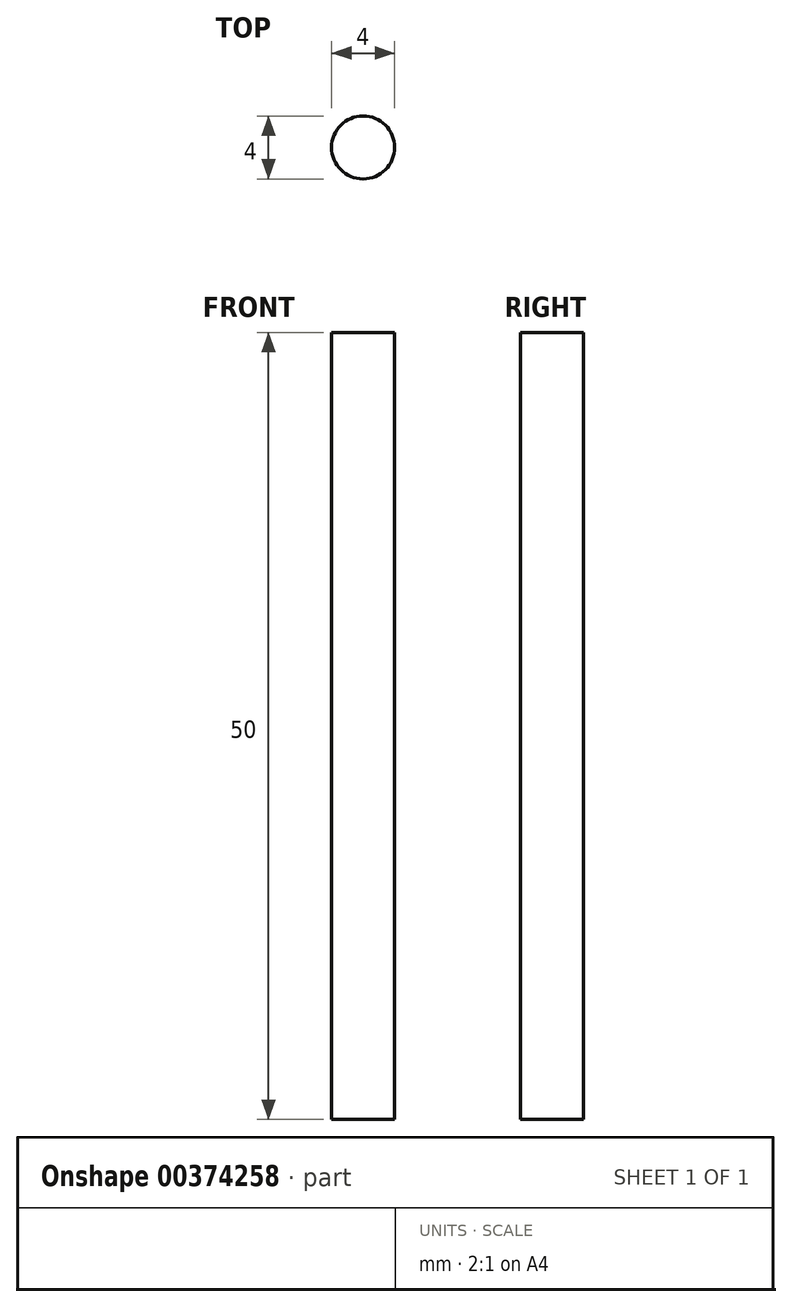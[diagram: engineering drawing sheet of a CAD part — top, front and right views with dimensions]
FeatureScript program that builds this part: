
annotation { "Feature Type Name" : "Feature", "Feature Type Description" : "" }
export const myFeature = defineFeature(function(context is Context, id is Id, definition is map)
    precondition{}
    {
        {
            var Q0;
            Q0=qCreatedBy(makeId("Top.planeOp"),FACE);
            var sketch = newSketch(context, id + "F0", { "sketchPlane" : qUnion([Q0])});
            skCircle(sketch, "E0", {"center": v(0, 0) * mm, "radius": 2 * mm});
            skSolve(sketch);
        }
        {
            var Q0;
            Q0=makeQuery(id+"F0.imprint","IMPRINT",FACE,{"disambiguationData":[TD([[makeQuery(id+"F0.imprint","IMPRINT",EDGE,{"derivedFrom":sQuery(id+"F0.wireOp",EDGE,"E0")}),1.0]])]});
            extrude(context, id + "F1", {"entities" : qUnion([Q0]), "depth" : 50 * mm});
        }
    });
